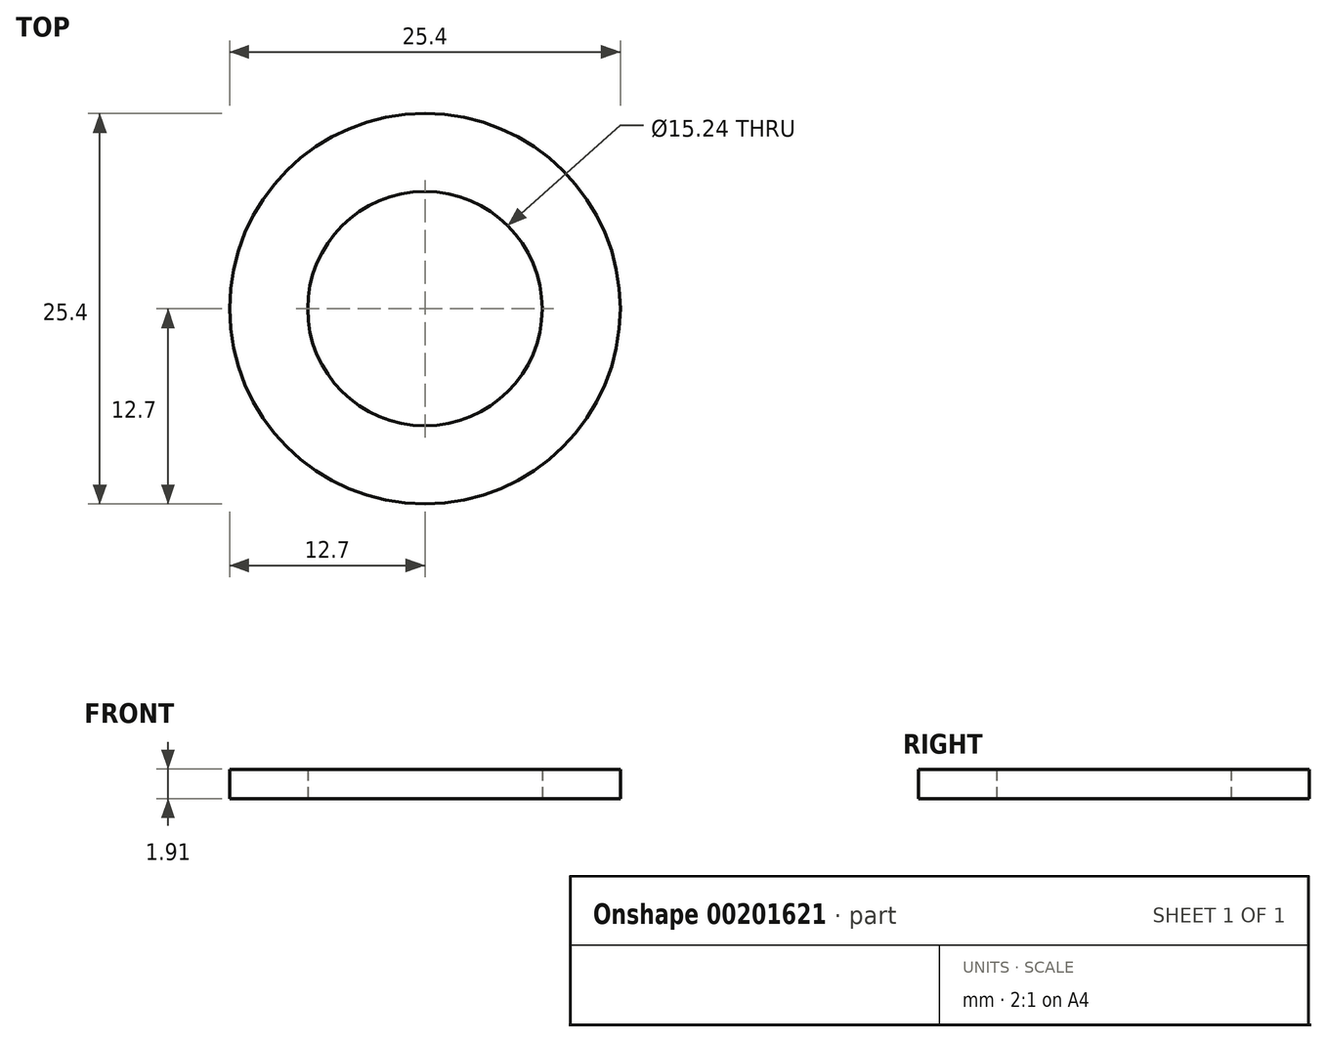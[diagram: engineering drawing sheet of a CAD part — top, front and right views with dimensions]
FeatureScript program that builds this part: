
annotation { "Feature Type Name" : "Feature", "Feature Type Description" : "" }
export const myFeature = defineFeature(function(context is Context, id is Id, definition is map)
    precondition{}
    {
        {
            var Q0;
            Q0=qCreatedBy(makeId("Top.planeOp"),FACE);
            var sketch = newSketch(context, id + "F0", { "sketchPlane" : qUnion([Q0])});
            skCircle(sketch, "E0", {"center": v(0, 0) * mm, "radius": 7.62 * mm});
            skCircle(sketch, "E1", {"center": v(0, 0) * mm, "radius": 12.7 * mm});
            skSolve(sketch);
        }
        {
            var Q0;
            Q0=makeQuery(id+"F0.imprint","IMPRINT",FACE,{"disambiguationData":[TD([[makeQuery(id+"F0.imprint","IMPRINT",EDGE,{"derivedFrom":sQuery(id+"F0.wireOp",EDGE,"E0")}),-1.0]])]});
            extrude(context, id + "F1", {"entities" : qUnion([Q0]), "depth" : 1.9 * mm});
        }
    });
